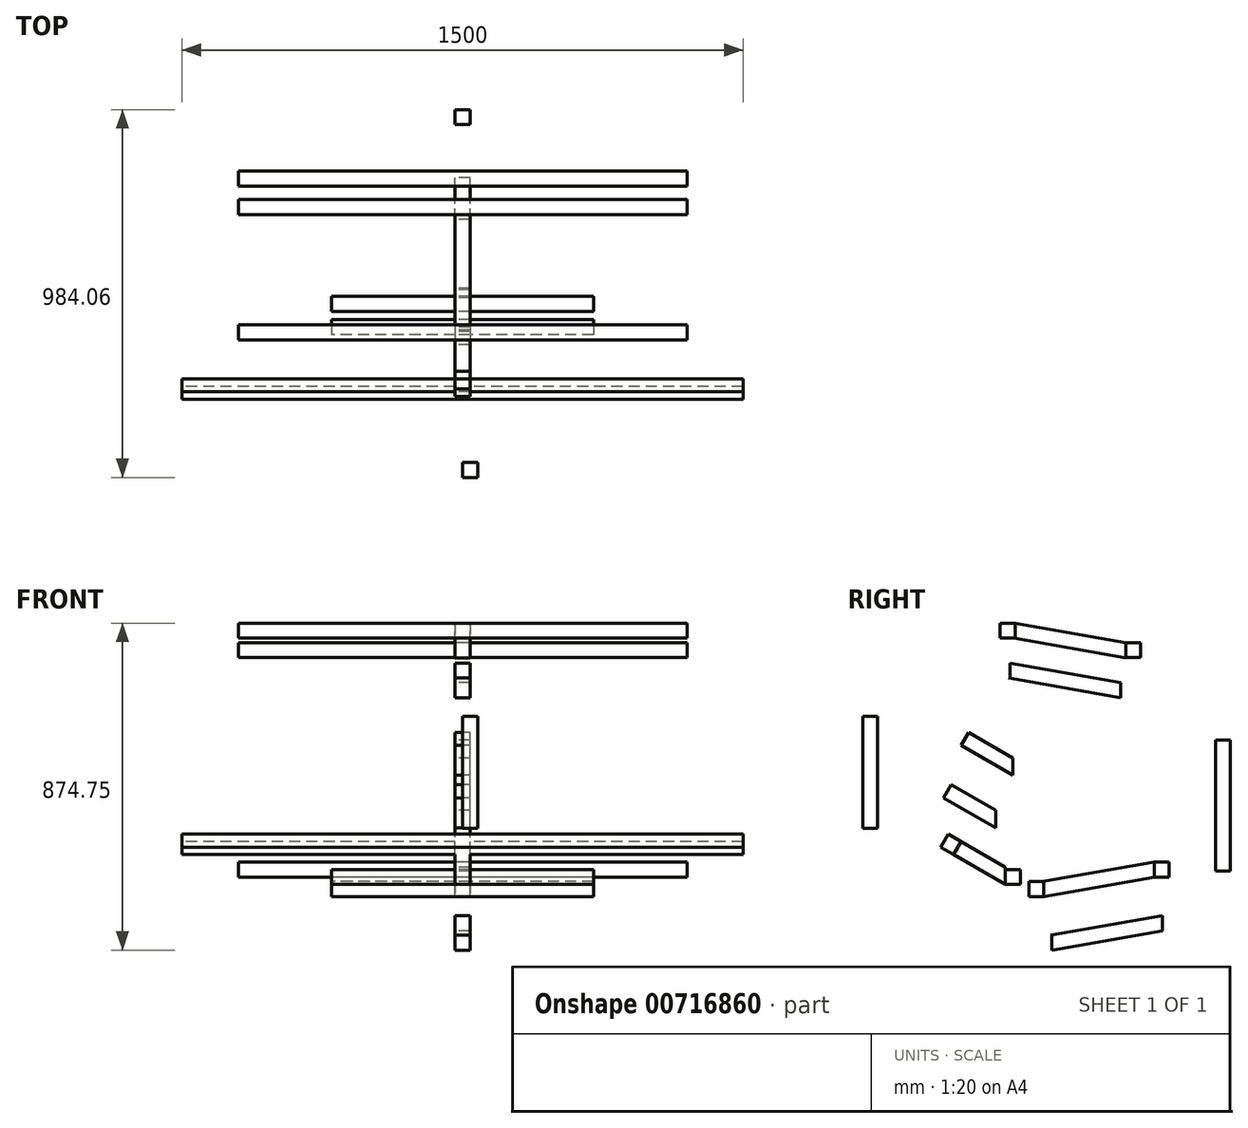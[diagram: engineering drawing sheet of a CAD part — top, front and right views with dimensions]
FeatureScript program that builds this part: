
annotation { "Feature Type Name" : "Feature", "Feature Type Description" : "" }
export const myFeature = defineFeature(function(context is Context, id is Id, definition is map)
    precondition{}
    {
        {
            var Q0;
            Q0=qCreatedBy(makeId("Right.planeOp"),FACE);
            var sketch = newSketch(context, id + "F0", { "sketchPlane" : qUnion([Q0])});
            skLineSegment(sketch, "E0.bottom", {"start": v(20, 20) * mm, "end": v(-20, 20) * mm});
            skLineSegment(sketch, "E0.top", {"start": v(20, -20) * mm, "end": v(-20, -20) * mm});
            skLineSegment(sketch, "E0.left", {"start": v(20, 20) * mm, "end": v(20, -20) * mm});
            skLineSegment(sketch, "E0.right", {"start": v(-20, 20) * mm, "end": v(-20, -20) * mm});
            skPoint(sketch, "E0.middle", {"position": v(0, 0) * mm});
            skLineSegment(sketch, "E1", {"start": v(-20, -20) * mm, "end": v(-193.2, 80) * mm});
            skLineSegment(sketch, "E2.0", {"start": v(-20, 26.19) * mm, "end": v(-173.2, 114.64) * mm});
            skLineSegment(sketch, "E3", {"start": v(-193.2, 80) * mm, "end": v(-173.2, 114.64) * mm});
            skLineSegment(sketch, "E4", {"start": v(-158.56, 60) * mm, "end": v(-138.56, 94.64) * mm});
            skLineSegment(sketch, "E5", {"start": v(-20, 26.19) * mm, "end": v(-20, 20) * mm});
            skSolve(sketch);
        }
        {
            var Q0;
            {var subQ1=sQuery(id+"F0.wireOp",EDGE,"E0.bottom");Q0=makeQuery(id+"F0.imprint","IMPRINT",FACE,{"disambiguationData":[TD([[makeQuery(id+"F0.imprint","IMPRINT",EDGE,{"derivedFrom":subQ1}),1.0]])]});}
            extrude(context, id + "F1", {"entities" : qUnion([Q0]), "endBound" : BoundingType.SYMMETRIC, "depth" : 700 * mm, "offsetDistance" : 25 * mm});
        }
        {
            var Q0;
            {var subQ5=sQuery(id+"F0.wireOp",EDGE,"E4");Q0=makeQuery(id+"F0.imprint","IMPRINT",FACE,{"disambiguationData":[TD([[makeQuery(id+"F0.imprint","IMPRINT",EDGE,{"derivedFrom":subQ5}),-1.0]])]});}
            extrude(context, id + "F2", {"entities" : qUnion([Q0]), "operationType" : NewBodyOperationType.ADD, "endBound" : BoundingType.SYMMETRIC, "depth" : 40 * mm, "offsetDistance" : 25 * mm});
        }
        {
            var Q0;
            {var subQ0=sQuery(id+"F0.wireOp",EDGE,"E3");Q0=makeQuery(id+"F0.imprint","IMPRINT",FACE,{"disambiguationData":[TD([[makeQuery(id+"F0.imprint","IMPRINT",EDGE,{"derivedFrom":subQ0}),-1.0]])]});}
            extrude(context, id + "F3", {"entities" : qUnion([Q0]), "operationType" : NewBodyOperationType.ADD, "endBound" : BoundingType.SYMMETRIC, "depth" : 1500 * mm, "offsetDistance" : 25 * mm});
        }
        {
            var Q0;
            Q0=qCreatedBy(makeId("Right.planeOp"),FACE);
            var sketch = newSketch(context, id + "F4", { "sketchPlane" : qUnion([Q0])});
            skLineSegment(sketch, "E6", {"start": v(-46.67, 132.07) * mm, "end": v(-46.67, 178.26) * mm});
            skLineSegment(sketch, "E7", {"start": v(-46.67, 132.07) * mm, "end": v(-185.24, 212.07) * mm});
            skLineSegment(sketch, "E8", {"start": v(-185.24, 212.07) * mm, "end": v(-165.24, 246.7) * mm});
            skLineSegment(sketch, "E9.0", {"start": v(-46.67, 178.26) * mm, "end": v(-165.24, 246.7) * mm});
            skSolve(sketch);
        }
        {
            var Q0;
            Q0 = qSketchRegion(id + "F4", true);
            extrude(context, id + "F5", {"entities" : qUnion([Q0]), "endBound" : BoundingType.SYMMETRIC, "depth" : 40 * mm, "offsetDistance" : 25 * mm});
        }
        {
            var Q0;
            Q0=makeQuery(id+"F5.opExtrude","SWEPT_BODY",BODY,{"disambiguationData":[OSD([sQuery(id+"F4.wireOp",EDGE,"E6"),sQuery(id+"F4.wireOp",EDGE,"E7"),sQuery(id+"F4.wireOp",EDGE,"E8"),sQuery(id+"F4.wireOp",EDGE,"E9.0")])]});
            transform(context, id + "F6", {"entities" : qUnion([Q0]), "transformType" : TransformType.TRANSLATION_3D, "dx" : 0 * mm, "dy" : 0 * mm, "dz" : 0 * mm, "makeCopy" : true});
        }
        {
            var Q0;
            Q0=qCreatedBy(makeId("Right.planeOp"),FACE);
            var sketch = newSketch(context, id + "F7", { "sketchPlane" : qUnion([Q0])});
            skLineSegment(sketch, "E10", {"start": v(0, 272.32) * mm, "end": v(0, 318.5) * mm});
            skLineSegment(sketch, "E11", {"start": v(0, 272.32) * mm, "end": v(-138.56, 352.32) * mm});
            skLineSegment(sketch, "E12.0", {"start": v(0, 318.5) * mm, "end": v(-118.56, 386.96) * mm});
            skLineSegment(sketch, "E13", {"start": v(-138.56, 352.32) * mm, "end": v(-118.56, 386.96) * mm});
            skSolve(sketch);
        }
        {
            var Q0;
            Q0 = qSketchRegion(id + "F7", true);
            extrude(context, id + "F8", {"entities" : qUnion([Q0]), "endBound" : BoundingType.SYMMETRIC, "depth" : 40 * mm, "offsetDistance" : 25 * mm});
        }
        {
            var Q0;
            Q0=qCreatedBy(makeId("Right.planeOp"),FACE);
            var sketch = newSketch(context, id + "F9", { "sketchPlane" : qUnion([Q0])});
            skLineSegment(sketch, "E14.bottom", {"start": v(42.42, -12.1) * mm, "end": v(82.42, -12.1) * mm});
            skLineSegment(sketch, "E14.top", {"start": v(42.42, -52.1) * mm, "end": v(82.42, -52.1) * mm});
            skLineSegment(sketch, "E14.left", {"start": v(42.42, -12.1) * mm, "end": v(42.42, -52.1) * mm});
            skLineSegment(sketch, "E14.right", {"start": v(82.42, -12.1) * mm, "end": v(82.42, -52.1) * mm});
            skLineSegment(sketch, "E15", {"start": v(82.42, -52.1) * mm, "end": v(377.86, 0) * mm});
            skLineSegment(sketch, "E16.0", {"start": v(78.92, -12.1) * mm, "end": v(377.86, 40.62) * mm});
            skLineSegment(sketch, "E17.bottom", {"start": v(377.86, 0) * mm, "end": v(417.86, 0) * mm});
            skLineSegment(sketch, "E17.top", {"start": v(377.86, 40) * mm, "end": v(417.86, 40) * mm});
            skLineSegment(sketch, "E17.left", {"start": v(377.86, 0) * mm, "end": v(377.86, 40) * mm});
            skLineSegment(sketch, "E17.right", {"start": v(417.86, 0) * mm, "end": v(417.86, 40) * mm});
            skLineSegment(sketch, "E18", {"start": v(377.86, 40) * mm, "end": v(377.86, 40.62) * mm});
            skLineSegment(sketch, "E19.bottom", {"start": v(417.86, 40) * mm, "end": v(377.86, 40) * mm});
            skLineSegment(sketch, "E19.top", {"start": v(417.86, 390) * mm, "end": v(377.86, 390) * mm});
            skLineSegment(sketch, "E19.left", {"start": v(417.86, 40) * mm, "end": v(417.86, 390) * mm});
            skLineSegment(sketch, "E19.right", {"start": v(377.86, 40) * mm, "end": v(377.86, 390) * mm});
            skSolve(sketch);
        }
        {
            var Q0;
            Q0=makeQuery(id+"F9.imprint","IMPRINT",FACE,{"disambiguationData":[TD([[makeQuery(id+"F9.imprint","IMPRINT",EDGE,{"derivedFrom":sQuery(id+"F9.wireOp",EDGE,"E14.top")}),1.0]])]});
            extrude(context, id + "F10", {"entities" : qUnion([Q0]), "endBound" : BoundingType.SYMMETRIC, "depth" : 700 * mm, "offsetDistance" : 25 * mm});
        }
        {
            var Q0;
            {var subQ0=sQuery(id+"F9.wireOp",EDGE,"E14.right");Q0=makeQuery(id+"F9.imprint","IMPRINT",FACE,{"disambiguationData":[TD([[makeQuery(id+"F9.imprint","IMPRINT",EDGE,{"derivedFrom":subQ0}),1.0]])]});}
            var Q1;
            Q1=makeQuery(id+"F9.imprint","IMPRINT",FACE,{"disambiguationData":[TD([[makeQuery(id+"F9.imprint","IMPRINT",EDGE,{"derivedFrom":sQuery(id+"F9.wireOp",EDGE,"E19.bottom")}),-1.0]])]});
            extrude(context, id + "F11", {"entities" : qUnion([Q0, Q1]), "operationType" : NewBodyOperationType.ADD, "endBound" : BoundingType.SYMMETRIC, "depth" : 40 * mm, "offsetDistance" : 25 * mm});
        }
        {
            var Q0;
            Q0=qCreatedBy(makeId("Right.planeOp"),FACE);
            var sketch = newSketch(context, id + "F12", { "sketchPlane" : qUnion([Q0])});
            skLineSegment(sketch, "E20.bottom", {"start": v(100.64, -155.51) * mm, "end": v(104.14, -155.51) * mm});
            skLineSegment(sketch, "E20.right", {"start": v(104.14, -155.51) * mm, "end": v(104.14, -195.51) * mm});
            skLineSegment(sketch, "E21", {"start": v(104.14, -195.51) * mm, "end": v(399.58, -143.42) * mm});
            skLineSegment(sketch, "E22.0", {"start": v(100.64, -155.51) * mm, "end": v(399.58, -102.8) * mm});
            skLineSegment(sketch, "E23", {"start": v(399.58, -102.8) * mm, "end": v(399.58, -143.42) * mm});
            skSolve(sketch);
        }
        {
            var Q0;
            Q0 = qSketchRegion(id + "F12", true);
            extrude(context, id + "F13", {"entities" : qUnion([Q0]), "endBound" : BoundingType.SYMMETRIC, "depth" : 40 * mm, "offsetDistance" : 25 * mm});
        }
        {
            var Q0;
            Q0=makeQuery(id+"F9.imprint","IMPRINT",FACE,{"disambiguationData":[TD([[makeQuery(id+"F9.imprint","IMPRINT",EDGE,{"derivedFrom":sQuery(id+"F9.wireOp",EDGE,"E17.bottom")}),1.0]])]});
            extrude(context, id + "F14", {"entities" : qUnion([Q0]), "operationType" : NewBodyOperationType.ADD, "endBound" : BoundingType.SYMMETRIC, "depth" : 1200 * mm, "offsetDistance" : 25 * mm});
        }
        {
            var Q0;
            Q0=qCreatedBy(makeId("Right.planeOp"),FACE);
            var sketch = newSketch(context, id + "F15", { "sketchPlane" : qUnion([Q0])});
            skLineSegment(sketch, "E24.bottom", {"start": v(541.86, 16.11) * mm, "end": v(581.86, 16.11) * mm});
            skLineSegment(sketch, "E24.top", {"start": v(541.86, 366.11) * mm, "end": v(581.86, 366.11) * mm});
            skLineSegment(sketch, "E24.left", {"start": v(541.86, 16.11) * mm, "end": v(541.86, 366.11) * mm});
            skLineSegment(sketch, "E24.right", {"start": v(581.86, 16.11) * mm, "end": v(581.86, 366.11) * mm});
            skSolve(sketch);
        }
        {
            var Q0;
            Q0 = qSketchRegion(id + "F15", true);
            extrude(context, id + "F16", {"entities" : qUnion([Q0]), "endBound" : BoundingType.SYMMETRIC, "depth" : 40 * mm, "offsetDistance" : 25 * mm});
        }
        {
            var Q0;
            Q0=qCreatedBy(makeId("Right.planeOp"),FACE);
            var sketch = newSketch(context, id + "F17", { "sketchPlane" : qUnion([Q0])});
            skLineSegment(sketch, "E25.bottom", {"start": v(341.47, 587.14) * mm, "end": v(301.47, 587.14) * mm});
            skLineSegment(sketch, "E25.top", {"start": v(341.47, 627.14) * mm, "end": v(301.47, 627.14) * mm});
            skLineSegment(sketch, "E25.left", {"start": v(341.47, 587.14) * mm, "end": v(341.47, 627.14) * mm});
            skLineSegment(sketch, "E25.right", {"start": v(301.47, 587.14) * mm, "end": v(301.47, 627.14) * mm});
            skLineSegment(sketch, "E26", {"start": v(301.47, 627.14) * mm, "end": v(6.03, 679.24) * mm});
            skLineSegment(sketch, "E27.bottom", {"start": v(6.03, 679.24) * mm, "end": v(-33.97, 679.24) * mm});
            skLineSegment(sketch, "E27.top", {"start": v(6.03, 639.24) * mm, "end": v(-33.97, 639.24) * mm});
            skLineSegment(sketch, "E27.left", {"start": v(6.03, 679.24) * mm, "end": v(6.03, 639.24) * mm});
            skLineSegment(sketch, "E27.right", {"start": v(-33.97, 679.24) * mm, "end": v(-33.97, 639.24) * mm});
            skLineSegment(sketch, "E28.0", {"start": v(301.47, 586.53) * mm, "end": v(2.53, 639.24) * mm});
            skLineSegment(sketch, "E29", {"start": v(301.47, 587.14) * mm, "end": v(301.47, 586.53) * mm});
            skSolve(sketch);
        }
        {
            var Q0;
            Q0=makeQuery(id+"F17.imprint","IMPRINT",FACE,{"disambiguationData":[TD([[makeQuery(id+"F17.imprint","IMPRINT",EDGE,{"derivedFrom":sQuery(id+"F17.wireOp",EDGE,"E25.right")}),1.0]])]});
            extrude(context, id + "F18", {"entities" : qUnion([Q0]), "endBound" : BoundingType.SYMMETRIC, "depth" : 40 * mm, "offsetDistance" : 25 * mm});
        }
        {
            var Q0;
            Q0=makeQuery(id+"F17.imprint","IMPRINT",FACE,{"disambiguationData":[TD([[makeQuery(id+"F17.imprint","IMPRINT",EDGE,{"derivedFrom":sQuery(id+"F17.wireOp",EDGE,"E27.bottom")}),1.0]])]});
            var Q1;
            Q1=makeQuery(id+"F17.imprint","IMPRINT",FACE,{"disambiguationData":[TD([[makeQuery(id+"F17.imprint","IMPRINT",EDGE,{"derivedFrom":sQuery(id+"F17.wireOp",EDGE,"E25.bottom")}),-1.0]])]});
            extrude(context, id + "F19", {"entities" : qUnion([Q0, Q1]), "operationType" : NewBodyOperationType.ADD, "endBound" : BoundingType.SYMMETRIC, "depth" : 1200 * mm, "offsetDistance" : 25 * mm});
        }
        {
            var Q0;
            Q0=qCreatedBy(makeId("Right.planeOp"),FACE);
            var sketch = newSketch(context, id + "F20", { "sketchPlane" : qUnion([Q0])});
            skLineSegment(sketch, "E30", {"start": v(287.77, 520.8) * mm, "end": v(-7.67, 572.89) * mm});
            skLineSegment(sketch, "E31.top", {"start": v(-7.67, 532.89) * mm, "end": v(-11.17, 532.89) * mm});
            skLineSegment(sketch, "E31.left", {"start": v(-7.67, 572.89) * mm, "end": v(-7.67, 532.89) * mm});
            skLineSegment(sketch, "E32.0", {"start": v(287.77, 480.18) * mm, "end": v(-11.17, 532.89) * mm});
            skLineSegment(sketch, "E33", {"start": v(287.77, 520.8) * mm, "end": v(287.77, 480.18) * mm});
            skSolve(sketch);
        }
        {
            var Q0;
            Q0 = qSketchRegion(id + "F20", true);
            extrude(context, id + "F21", {"entities" : qUnion([Q0]), "endBound" : BoundingType.SYMMETRIC, "depth" : 40 * mm, "offsetDistance" : 25 * mm});
        }
        {
            var Q0;
            Q0=qCreatedBy(makeId("Right.planeOp"),FACE);
            var sketch = newSketch(context, id + "F22", { "sketchPlane" : qUnion([Q0])});
            skLineSegment(sketch, "E34.bottom", {"start": v(-402.2, 130.5) * mm, "end": v(-362.2, 130.5) * mm});
            skLineSegment(sketch, "E34.top", {"start": v(-402.2, 430.5) * mm, "end": v(-362.2, 430.5) * mm});
            skLineSegment(sketch, "E34.left", {"start": v(-402.2, 130.5) * mm, "end": v(-402.2, 430.5) * mm});
            skLineSegment(sketch, "E34.right", {"start": v(-362.2, 130.5) * mm, "end": v(-362.2, 430.5) * mm});
            skSolve(sketch);
        }
        {
            var Q0;
            Q0 = qSketchRegion(id + "F22", true);
            extrude(context, id + "F23", {"entities" : qUnion([Q0]), "depth" : 40 * mm, "offsetDistance" : 25 * mm});
        }
    });
